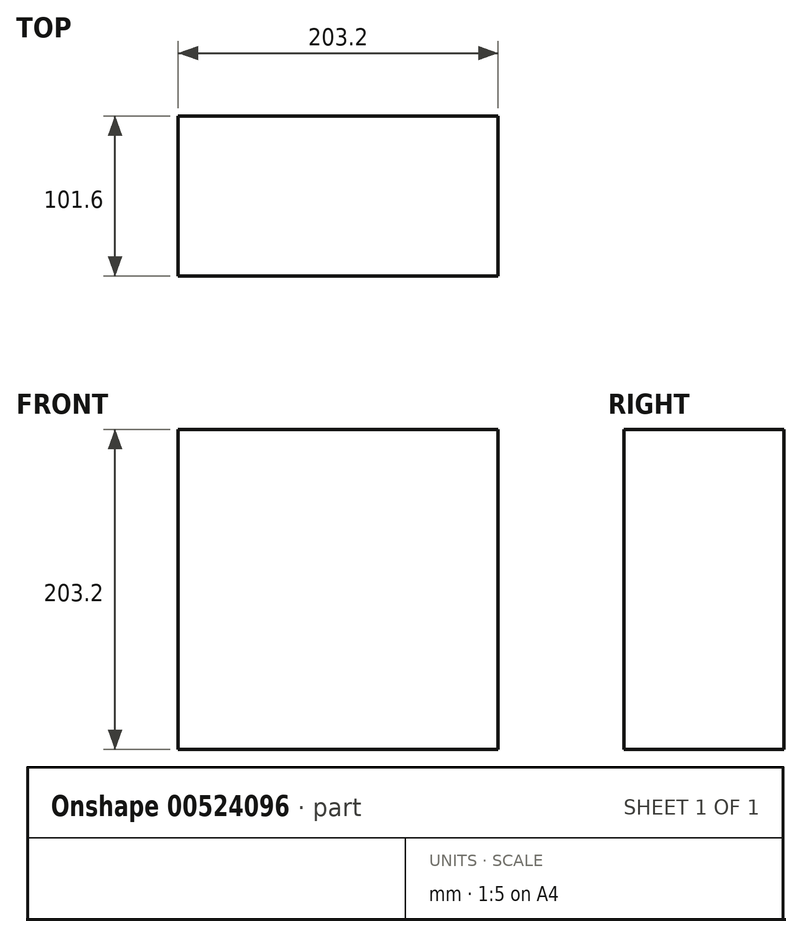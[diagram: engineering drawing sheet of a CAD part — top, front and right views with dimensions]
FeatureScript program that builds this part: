
annotation { "Feature Type Name" : "Feature", "Feature Type Description" : "" }
export const myFeature = defineFeature(function(context is Context, id is Id, definition is map)
    precondition{}
    {
        {
            var Q0;
            Q0=qCreatedBy(makeId("Top.planeOp"),FACE);
            var sketch = newSketch(context, id + "F0", { "sketchPlane" : qUnion([Q0])});
            skLineSegment(sketch, "E0.bottom", {"start": v(-101.6, 50.8) * mm, "end": v(101.6, 50.8) * mm});
            skLineSegment(sketch, "E0.top", {"start": v(-101.6, -50.8) * mm, "end": v(101.6, -50.8) * mm});
            skLineSegment(sketch, "E0.left", {"start": v(-101.6, 50.8) * mm, "end": v(-101.6, -50.8) * mm});
            skLineSegment(sketch, "E0.right", {"start": v(101.6, 50.8) * mm, "end": v(101.6, -50.8) * mm});
            skSolve(sketch);
        }
        {
            var Q0;
            Q0=makeQuery(id+"F0.imprint","IMPRINT",FACE,{"disambiguationData":[TD([[makeQuery(id+"F0.imprint","IMPRINT",EDGE,{"derivedFrom":sQuery(id+"F0.wireOp",EDGE,"E0.bottom")}),-1.0]])]});
            extrude(context, id + "F1", {"entities" : qUnion([Q0]), "depth" : 203.2 * mm, "offsetDistance" : 25.4 * mm});
        }
    });
